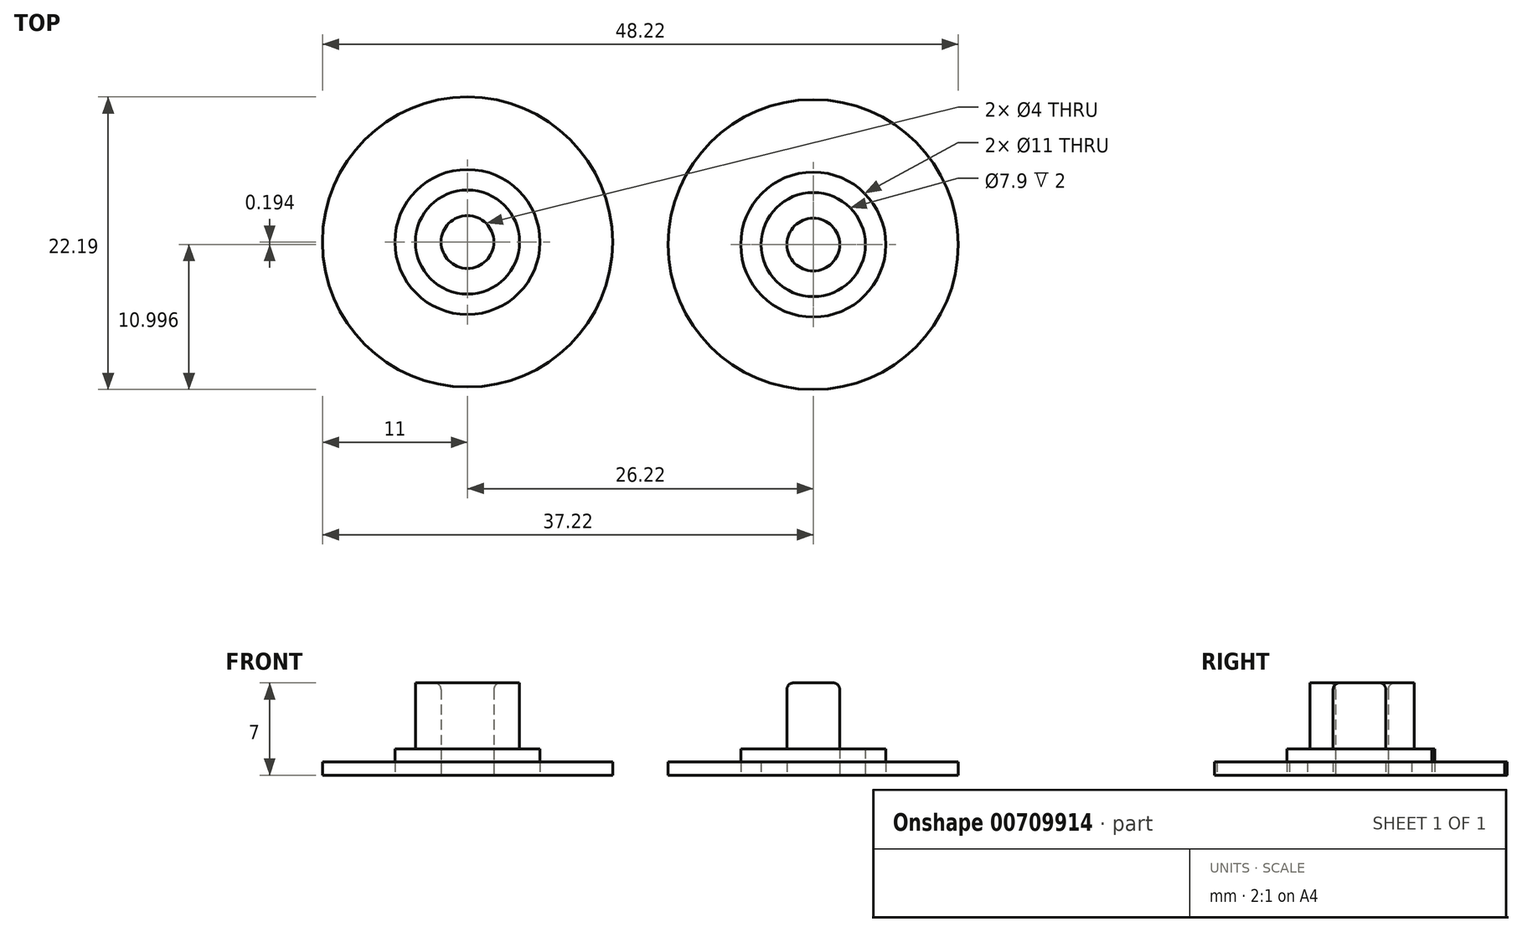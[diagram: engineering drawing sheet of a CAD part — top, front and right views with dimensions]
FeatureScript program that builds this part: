
annotation { "Feature Type Name" : "Feature", "Feature Type Description" : "" }
export const myFeature = defineFeature(function(context is Context, id is Id, definition is map)
    precondition{}
    {
        {
            var Q0;
            Q0=qCreatedBy(makeId("Top.planeOp"),FACE);
            var sketch = newSketch(context, id + "F0", { "sketchPlane" : qUnion([Q0])});
            skCircle(sketch, "E0", {"center": v(0, 0) * mm, "radius": 11 * mm});
            skCircle(sketch, "E1", {"center": v(0, 0) * mm, "radius": 5.5 * mm});
            skCircle(sketch, "E2", {"center": v(0, 0) * mm, "radius": 3.95 * mm});
            skCircle(sketch, "E3", {"center": v(0, 0) * mm, "radius": 2 * mm});
            skCircle(sketch, "E4", {"center": v(26.22, -0.2) * mm, "radius": 11 * mm});
            skCircle(sketch, "E5", {"center": v(26.22, -0.2) * mm, "radius": 5.5 * mm});
            skCircle(sketch, "E6", {"center": v(26.22, -0.2) * mm, "radius": 3.95 * mm});
            skCircle(sketch, "E7", {"center": v(26.22, -0.2) * mm, "radius": 2 * mm});
            skSolve(sketch);
        }
        {
            var Q0;
            Q0=makeQuery(id+"F0.imprint","IMPRINT",FACE,{"disambiguationData":[TD([[makeQuery(id+"F0.imprint","IMPRINT",EDGE,{"derivedFrom":sQuery(id+"F0.wireOp",EDGE,"E0")}),1.0]])]});
            var Q1;
            Q1=makeQuery(id+"F0.imprint","IMPRINT",FACE,{"disambiguationData":[TD([[makeQuery(id+"F0.imprint","IMPRINT",EDGE,{"derivedFrom":sQuery(id+"F0.wireOp",EDGE,"E4")}),1.0]])]});
            extrude(context, id + "F1", {"entities" : qUnion([Q0, Q1]), "depth" : 1 * mm, "offsetDistance" : 25 * mm});
        }
        {
            var Q0;
            Q0=makeQuery(id+"F0.imprint","IMPRINT",FACE,{"disambiguationData":[TD([[makeQuery(id+"F0.imprint","IMPRINT",EDGE,{"derivedFrom":sQuery(id+"F0.wireOp",EDGE,"E1")}),1.0]])]});
            var Q1;
            Q1=makeQuery(id+"F0.imprint","IMPRINT",FACE,{"disambiguationData":[TD([[makeQuery(id+"F0.imprint","IMPRINT",EDGE,{"derivedFrom":sQuery(id+"F0.wireOp",EDGE,"E5")}),1.0]])]});
            extrude(context, id + "F2", {"entities" : qUnion([Q0, Q1]), "depth" : 2 * mm, "offsetDistance" : 25 * mm});
        }
        {
            var Q0;
            Q0=makeQuery(id+"F0.imprint","IMPRINT",FACE,{"disambiguationData":[TD([[makeQuery(id+"F0.imprint","IMPRINT",EDGE,{"derivedFrom":sQuery(id+"F0.wireOp",EDGE,"E2")}),1.0]])]});
            var Q1;
            Q1=makeQuery(id+"F0.imprint","IMPRINT",FACE,{"disambiguationData":[TD([[makeQuery(id+"F0.imprint","IMPRINT",EDGE,{"derivedFrom":sQuery(id+"F0.wireOp",EDGE,"E7")}),1.0]])]});
            extrude(context, id + "F3", {"entities" : qUnion([Q0, Q1]), "operationType" : NewBodyOperationType.ADD, "depth" : 7 * mm, "offsetDistance" : 25 * mm});
        }
        {
            var Q0;
            Q0=makeQuery(id+"F0.imprint","IMPRINT",FACE,{"disambiguationData":[TD([[makeQuery(id+"F0.imprint","IMPRINT",EDGE,{"derivedFrom":sQuery(id+"F0.wireOp",EDGE,"E6")}),1.0]])]});
            var Q1;
            Q1=makeQuery(id+"F0.imprint","IMPRINT",FACE,{"disambiguationData":[TD([[makeQuery(id+"F0.imprint","IMPRINT",EDGE,{"derivedFrom":sQuery(id+"F0.wireOp",EDGE,"E3")}),1.0]])]});
            extrude(context, id + "F4", {"entities" : qUnion([Q0, Q1]), "depth" : 1 * mm, "offsetDistance" : 25 * mm});
        }
        {
            var Q0;
            Q0=makeQuery(id+"F3.opExtrude","CAP_EDGE",EDGE,{"disambiguationData":[OSD([sQuery(id+"F0.wireOp",EDGE,"E3")])],"isStart":false});
            var Q1;
            Q1=makeQuery(id+"F3.opExtrude","CAP_EDGE",EDGE,{"disambiguationData":[OSD([sQuery(id+"F0.wireOp",EDGE,"E7")])],"isStart":false});
            fillet(context, id + "F5", {"entities" : qUnion([Q0, Q1]), "radius" : .5 * mm, "tangentPropagation" : true, "allowEdgeOverflow" : false});
        }
    });
